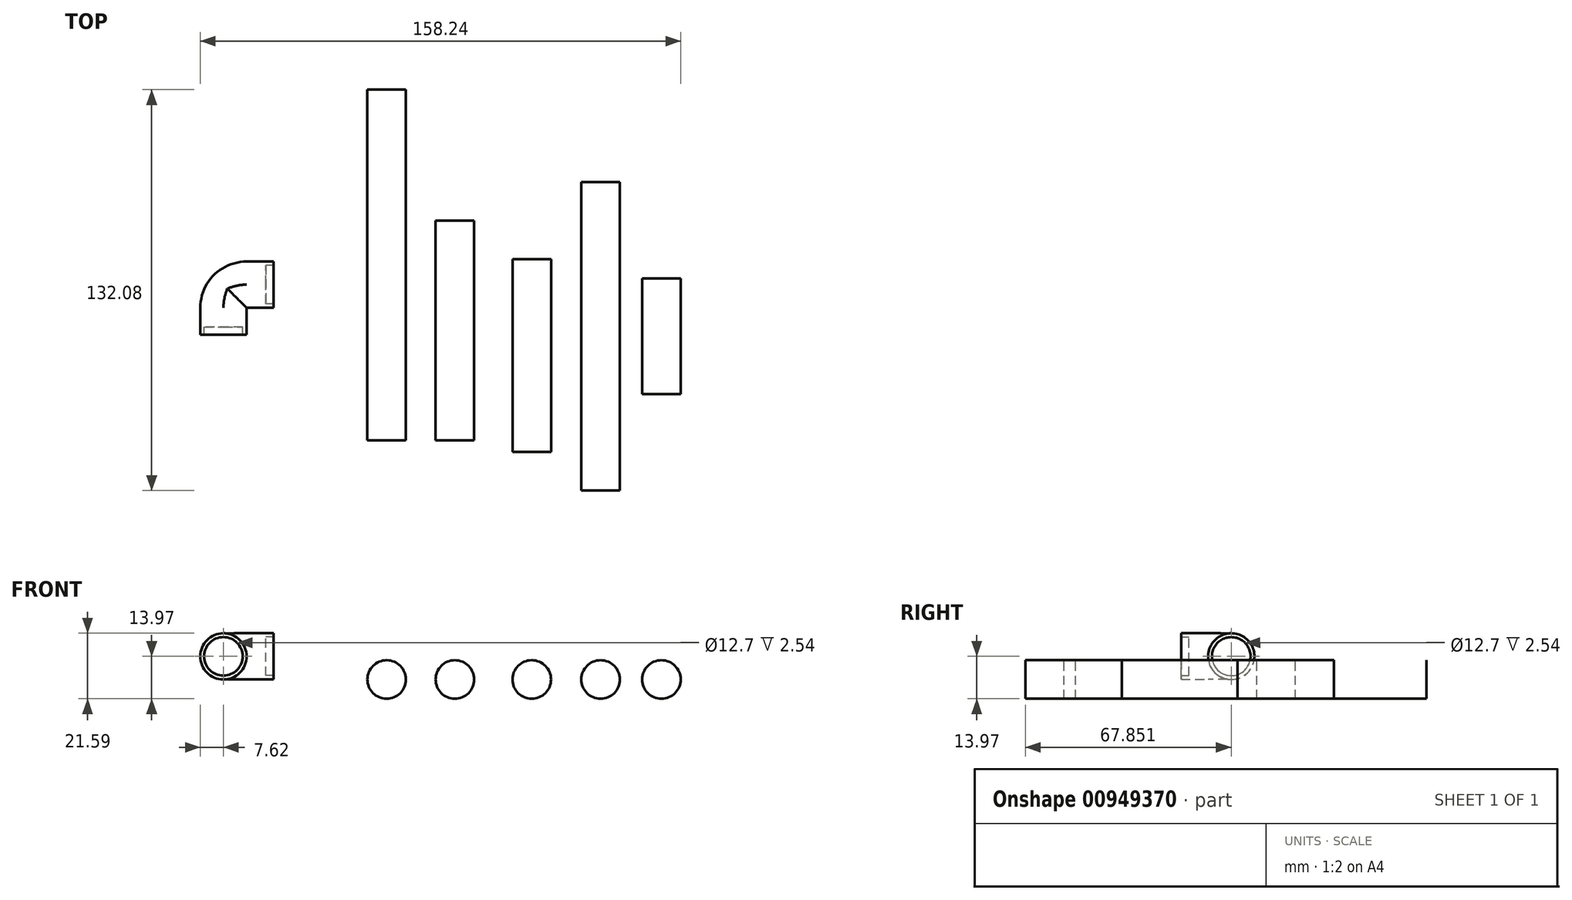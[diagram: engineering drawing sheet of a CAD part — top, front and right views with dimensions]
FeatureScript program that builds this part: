
annotation { "Feature Type Name" : "Feature", "Feature Type Description" : "" }
export const myFeature = defineFeature(function(context is Context, id is Id, definition is map)
    precondition{}
    {
        {
            var Q0;
            Q0=qCreatedBy(makeId("Front.planeOp"),FACE);
            var sketch = newSketch(context, id + "F0", { "sketchPlane" : qUnion([Q0])});
            skCircle(sketch, "E0", {"center": v(0, 0) * mm, "radius": 6.35 * mm});
            skSolve(sketch);
        }
        {
            var Q0;
            Q0=makeQuery(id+"F0.imprint","IMPRINT",FACE,{"disambiguationData":[TD([[makeQuery(id+"F0.imprint","IMPRINT",EDGE,{"derivedFrom":sQuery(id+"F0.wireOp",EDGE,"E0")}),1.0]])]});
            extrude(context, id + "F1", {"entities" : qUnion([Q0]), "depth" : 38.1 * mm, "offsetDistance" : 25.4 * mm, "hasSecondDirection" : true, "secondDirectionOppositeDirection" : true, "secondDirectionDepth" : 25.4 * mm});
        }
        {
            var Q0;
            Q0=qCreatedBy(makeId("Top.planeOp"),FACE);
            var sketch = newSketch(context, id + "F2", { "sketchPlane" : qUnion([Q0])});
            skLineSegment(sketch, "E1.top", {"start": v(-109.17, 3.08) * mm, "end": v(-93.93, 3.08) * mm});
            skLineSegment(sketch, "E1.left", {"start": v(-109.17, 9.43) * mm, "end": v(-109.17, 3.08) * mm});
            skLineSegment(sketch, "E1.right", {"start": v(-93.93, 9.43) * mm, "end": v(-93.93, 3.08) * mm});
            skArc(sketch, "E2", {"start": v(-93.93, 24.67) * mm, "mid": v(-104.7, 20.2) * mm, "end": v(-109.17, 9.43) * mm});
            skLineSegment(sketch, "E3.bottom", {"start": v(-93.93, 24.67) * mm, "end": v(-87.58, 24.67) * mm});
            skLineSegment(sketch, "E3.top", {"start": v(-93.93, 9.43) * mm, "end": v(-87.58, 9.43) * mm});
            skLineSegment(sketch, "E3.right", {"start": v(-87.58, 24.67) * mm, "end": v(-87.58, 9.43) * mm});
            skSolve(sketch);
        }
        {
            var Q0;
            Q0=makeQuery(id+"F2.imprint","IMPRINT",FACE,{"disambiguationData":[TD([[makeQuery(id+"F2.imprint","IMPRINT",EDGE,{"derivedFrom":sQuery(id+"F2.wireOp",EDGE,"E1.top")}),1.0]])]});
            extrude(context, id + "F3", {"entities" : qUnion([Q0]), "depth" : 15.24 * mm, "offsetDistance" : 25.4 * mm});
        }
        {
            var Q0;
            Q0=qCreatedBy(makeId("Front.planeOp"),FACE);
            var sketch = newSketch(context, id + "F4", { "sketchPlane" : qUnion([Q0])});
            skCircle(sketch, "E4", {"center": v(22.69, 0) * mm, "radius": 6.35 * mm});
            skSolve(sketch);
        }
        {
            var Q0;
            Q0=makeQuery(id+"F4.imprint","IMPRINT",FACE,{"disambiguationData":[TD([[makeQuery(id+"F4.imprint","IMPRINT",EDGE,{"derivedFrom":sQuery(id+"F4.wireOp",EDGE,"E4")}),1.0]])]});
            extrude(context, id + "F5", {"entities" : qUnion([Q0]), "depth" : 50.8 * mm, "offsetDistance" : 25.4 * mm, "hasSecondDirection" : true, "secondDirectionOppositeDirection" : true, "secondDirectionDepth" : 50.8 * mm});
        }
        {
            var Q0;
            Q0=qCreatedBy(makeId("Front.planeOp"),FACE);
            var sketch = newSketch(context, id + "F6", { "sketchPlane" : qUnion([Q0])});
            skCircle(sketch, "E5", {"center": v(42.72, 0) * mm, "radius": 6.35 * mm});
            skSolve(sketch);
        }
        {
            var Q0;
            Q0=makeQuery(id+"F6.imprint","IMPRINT",FACE,{"disambiguationData":[TD([[makeQuery(id+"F6.imprint","IMPRINT",EDGE,{"derivedFrom":sQuery(id+"F6.wireOp",EDGE,"E5")}),1.0]])]});
            extrude(context, id + "F7", {"entities" : qUnion([Q0]), "depth" : 19.05 * mm, "offsetDistance" : 25.4 * mm, "hasSecondDirection" : true, "secondDirectionOppositeDirection" : true, "secondDirectionDepth" : 19.05 * mm});
        }
        {
            var Q0;
            Q0=makeQuery(id+"F3.opExtrude","CAP_EDGE",EDGE,{"disambiguationData":[OSD([sQuery(id+"F2.wireOp",EDGE,"E2")])],"isStart":false});
            var Q1;
            Q1=makeQuery(id+"F3.opExtrude","CAP_EDGE",EDGE,{"disambiguationData":[OSD([sQuery(id+"F2.wireOp",EDGE,"E1.left")])],"isStart":false});
            var Q2;
            Q2=makeQuery(id+"F3.opExtrude","CAP_EDGE",EDGE,{"disambiguationData":[OSD([sQuery(id+"F2.wireOp",EDGE,"E3.top")])],"isStart":false});
            var Q3;
            Q3=makeQuery(id+"F3.opExtrude","CAP_EDGE",EDGE,{"disambiguationData":[OSD([sQuery(id+"F2.wireOp",EDGE,"E1.right")])],"isStart":false});
            var Q4;
            Q4=makeQuery(id+"F3.opExtrude","CAP_EDGE",EDGE,{"disambiguationData":[OSD([sQuery(id+"F2.wireOp",EDGE,"E1.left")])],"isStart":true});
            var Q5;
            Q5=makeQuery(id+"F3.opExtrude","CAP_EDGE",EDGE,{"disambiguationData":[OSD([sQuery(id+"F2.wireOp",EDGE,"E1.right")])],"isStart":true});
            var Q6;
            Q6=makeQuery(id+"F3.opExtrude","CAP_EDGE",EDGE,{"disambiguationData":[OSD([sQuery(id+"F2.wireOp",EDGE,"E3.top")])],"isStart":true});
            fillet(context, id + "F8", {"entities" : qUnion([Q0, Q1, Q2, Q3, Q4, Q5, Q6]), "radius" : 7.62 * mm, "tangentPropagation" : true, "allowEdgeOverflow" : false});
        }
        {
            var Q0;
            Q0=makeQuery(id+"F3.opExtrude","SWEPT_FACE",FACE,{"disambiguationData":[OSD([sQuery(id+"F2.wireOp",EDGE,"E1.top")])]});
            var sketch = newSketch(context, id + "F9", { "sketchPlane" : qUnion([Q0])});
            skCircle(sketch, "E6", {"center": v(-101.55, 7.62) * mm, "radius": 6.35 * mm});
            skSolve(sketch);
        }
        {
            var Q0;
            Q0=makeQuery(id+"F9.imprint","IMPRINT",FACE,{"disambiguationData":[TD([[makeQuery(id+"F9.imprint","IMPRINT",EDGE,{"derivedFrom":sQuery(id+"F9.wireOp",EDGE,"E6")}),-1.0]])]});
            extrude(context, id + "F10", {"entities" : qUnion([Q0]), "operationType" : NewBodyOperationType.ADD, "depth" : 2.54 * mm, "offsetDistance" : 25.4 * mm});
        }
        {
            var Q0;
            Q0=makeQuery(id+"F3.opExtrude","SWEPT_FACE",FACE,{"disambiguationData":[OSD([sQuery(id+"F2.wireOp",EDGE,"E3.right")])]});
            var sketch = newSketch(context, id + "F11", { "sketchPlane" : qUnion([Q0])});
            skCircle(sketch, "E7", {"center": v(17.05, 7.62) * mm, "radius": 6.35 * mm});
            skSolve(sketch);
        }
        {
            var Q0;
            Q0=makeQuery(id+"F11.imprint","IMPRINT",FACE,{"disambiguationData":[TD([[makeQuery(id+"F11.imprint","IMPRINT",EDGE,{"derivedFrom":sQuery(id+"F11.wireOp",EDGE,"E7")}),-1.0]])]});
            extrude(context, id + "F12", {"entities" : qUnion([Q0]), "operationType" : NewBodyOperationType.ADD, "depth" : 2.54 * mm, "offsetDistance" : 25.4 * mm});
        }
        {
            var Q0;
            Q0=qCreatedBy(makeId("Front.planeOp"),FACE);
            var sketch = newSketch(context, id + "F13", { "sketchPlane" : qUnion([Q0])});
            skCircle(sketch, "E8", {"center": v(-25.3, 0) * mm, "radius": 6.35 * mm});
            skSolve(sketch);
        }
        {
            var Q0;
            Q0=makeQuery(id+"F13.imprint","IMPRINT",FACE,{"disambiguationData":[TD([[makeQuery(id+"F13.imprint","IMPRINT",EDGE,{"derivedFrom":sQuery(id+"F13.wireOp",EDGE,"E8")}),1.0]])]});
            extrude(context, id + "F14", {"entities" : qUnion([Q0]), "depth" : 34.3 * mm, "offsetDistance" : 25.4 * mm, "hasSecondDirection" : true, "secondDirectionOppositeDirection" : true, "secondDirectionDepth" : 38.1 * mm});
        }
        {
            var Q0;
            Q0=qCreatedBy(makeId("Front.planeOp"),FACE);
            var sketch = newSketch(context, id + "F15", { "sketchPlane" : qUnion([Q0])});
            skCircle(sketch, "E9", {"center": v(-47.78, 0) * mm, "radius": 6.35 * mm});
            skSolve(sketch);
        }
        {
            var Q0;
            Q0=makeQuery(id+"F15.imprint","IMPRINT",FACE,{"disambiguationData":[TD([[makeQuery(id+"F15.imprint","IMPRINT",EDGE,{"derivedFrom":sQuery(id+"F15.wireOp",EDGE,"E9")}),1.0]])]});
            extrude(context, id + "F16", {"entities" : qUnion([Q0]), "depth" : 34.3 * mm, "offsetDistance" : 25.4 * mm, "hasSecondDirection" : true, "secondDirectionOppositeDirection" : true, "secondDirectionDepth" : 81.28 * mm});
        }
    });
